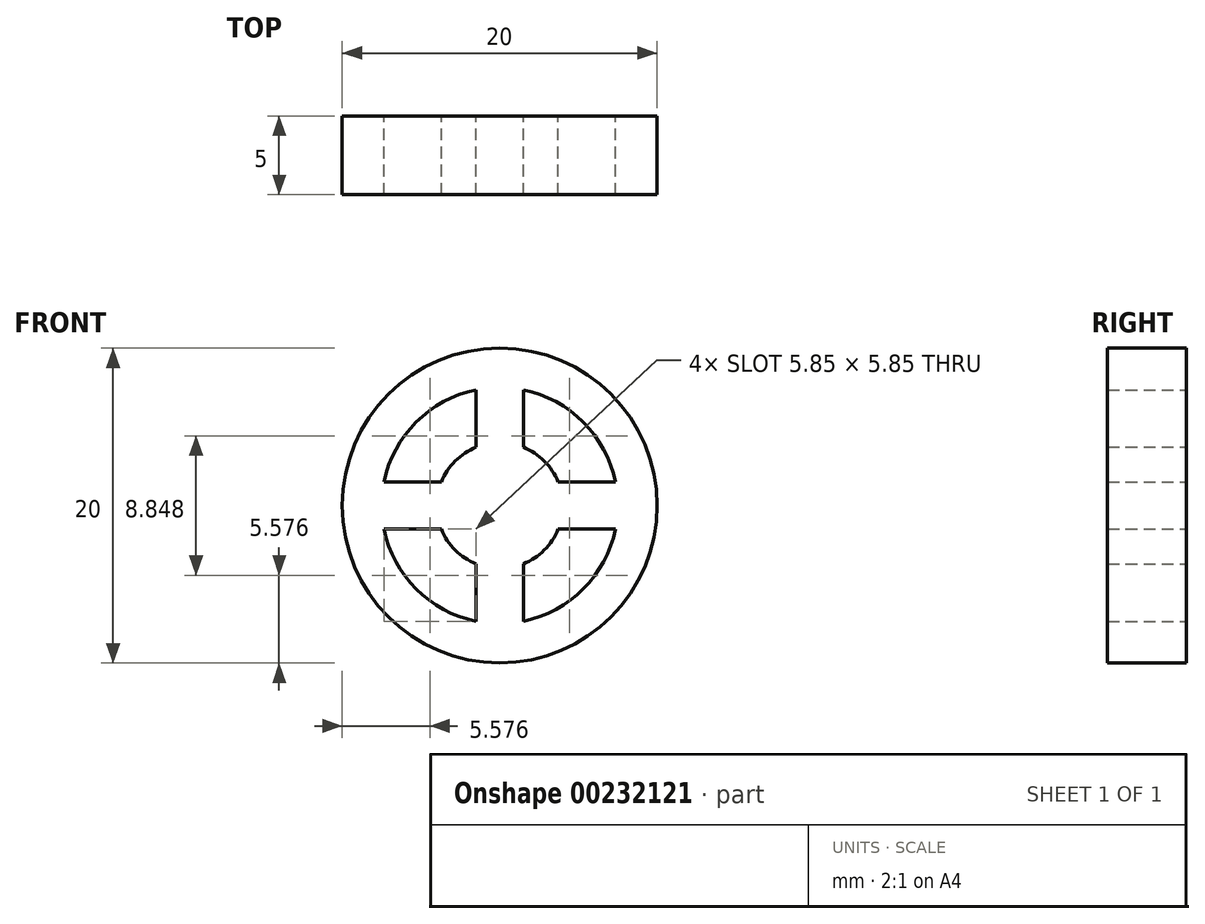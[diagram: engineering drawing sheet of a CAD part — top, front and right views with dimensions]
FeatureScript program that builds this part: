
annotation { "Feature Type Name" : "Feature", "Feature Type Description" : "" }
export const myFeature = defineFeature(function(context is Context, id is Id, definition is map)
    precondition{}
    {
        {
            var Q0;
            Q0=qCreatedBy(makeId("Front.planeOp"),FACE);
            var sketch = newSketch(context, id + "F0", { "sketchPlane" : qUnion([Q0])});
            skCircle(sketch, "E0", {"center": v(0, 0) * mm, "radius": 10 * mm});
            skArc(sketch, "E1", {"start": v(-1.5, 3.7) * mm, "mid": v(-2.83, 2.83) * mm, "end": v(-3.7, 1.5) * mm});
            skArc(sketch, "E2", {"start": v(-1.5, 7.35) * mm, "mid": v(-5.3, 5.3) * mm, "end": v(-7.35, 1.5) * mm});
            skLineSegment(sketch, "E3.left", {"start": v(1.5, 7.35) * mm, "end": v(1.5, 3.7) * mm});
            skLineSegment(sketch, "E3.right", {"start": v(-1.5, 7.35) * mm, "end": v(-1.5, 3.7) * mm});
            skLineSegment(sketch, "E4.bottom", {"start": v(7.35, 1.5) * mm, "end": v(3.7, 1.5) * mm});
            skLineSegment(sketch, "E4.top", {"start": v(7.35, -1.5) * mm, "end": v(3.7, -1.5) * mm});
            skLineSegment(sketch, "E5.trimOffspring", {"start": v(-3.7, 1.5) * mm, "end": v(-7.35, 1.5) * mm});
            skLineSegment(sketch, "E6.trimOffspring", {"start": v(-1.5, -3.7) * mm, "end": v(-1.5, -7.35) * mm});
            skLineSegment(sketch, "E7.trimOffspring", {"start": v(1.5, -3.7) * mm, "end": v(1.5, -7.35) * mm});
            skArc(sketch, "E8.trimOffspring", {"start": v(-7.35, -1.5) * mm, "mid": v(-5.3, -5.3) * mm, "end": v(-1.5, -7.35) * mm});
            skArc(sketch, "E9.trimOffspring", {"start": v(7.35, 1.5) * mm, "mid": v(5.3, 5.3) * mm, "end": v(1.5, 7.35) * mm});
            skArc(sketch, "E10.trimOffspring", {"start": v(1.5, -7.35) * mm, "mid": v(5.3, -5.3) * mm, "end": v(7.35, -1.5) * mm});
            skArc(sketch, "E11.trimOffspring", {"start": v(1.5, -3.7) * mm, "mid": v(2.83, -2.83) * mm, "end": v(3.7, -1.5) * mm});
            skArc(sketch, "E12.trimOffspring", {"start": v(3.7, 1.5) * mm, "mid": v(2.83, 2.83) * mm, "end": v(1.5, 3.7) * mm});
            skArc(sketch, "E13.trimOffspring", {"start": v(-3.7, -1.5) * mm, "mid": v(-2.83, -2.83) * mm, "end": v(-1.5, -3.7) * mm});
            skLineSegment(sketch, "E14.trimOffspring", {"start": v(-3.7, -1.5) * mm, "end": v(-7.35, -1.5) * mm});
            skSolve(sketch);
        }
        {
            var Q0;
            Q0 = qSketchRegion(id + "F0", true);
            extrude(context, id + "F1", {"entities" : qUnion([Q0]), "depth" : 5 * mm});
        }
    });
